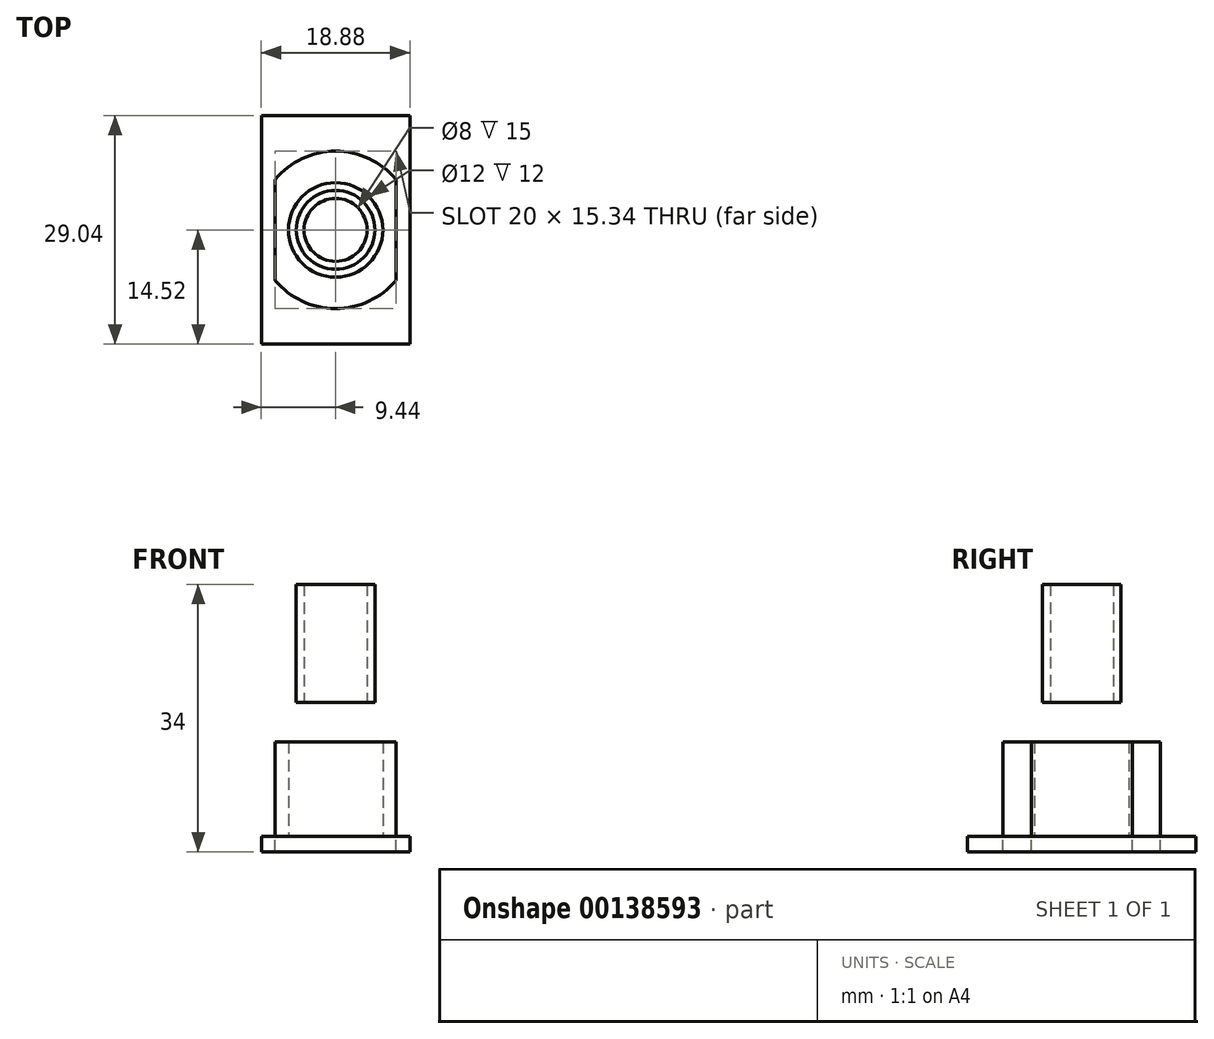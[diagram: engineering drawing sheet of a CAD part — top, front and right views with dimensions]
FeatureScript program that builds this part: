
annotation { "Feature Type Name" : "Feature", "Feature Type Description" : "" }
export const myFeature = defineFeature(function(context is Context, id is Id, definition is map)
    precondition{}
    {
        {
            var Q0;
            Q0=qCreatedBy(makeId("Top.planeOp"),FACE);
            var sketch = newSketch(context, id + "F0", { "sketchPlane" : qUnion([Q0])});
            skArc(sketch, "E0", {"start": v(-7.67, -6.42) * mm, "mid": v(0, -10) * mm, "end": v(7.67, -6.42) * mm});
            skLineSegment(sketch, "E1.left", {"start": v(7.67, 6.42) * mm, "end": v(7.67, -6.42) * mm});
            skLineSegment(sketch, "E1.right", {"start": v(-7.67, 6.42) * mm, "end": v(-7.67, -6.42) * mm});
            skArc(sketch, "E2.trimOffspring", {"start": v(7.67, 6.42) * mm, "mid": v(0, 10) * mm, "end": v(-7.67, 6.42) * mm});
            skCircle(sketch, "E3", {"center": v(0, 0) * mm, "radius": 6 * mm});
            skLineSegment(sketch, "E4.bottom", {"start": v(9.44, 14.52) * mm, "end": v(-9.44, 14.52) * mm});
            skLineSegment(sketch, "E4.top", {"start": v(9.44, -14.52) * mm, "end": v(-9.44, -14.52) * mm});
            skLineSegment(sketch, "E4.left", {"start": v(9.44, 14.52) * mm, "end": v(9.44, -14.52) * mm});
            skLineSegment(sketch, "E4.right", {"start": v(-9.44, 14.52) * mm, "end": v(-9.44, -14.52) * mm});
            skSolve(sketch);
        }
        {
            var Q0;
            Q0=makeQuery(id+"F0.imprint","IMPRINT",FACE,{"disambiguationData":[TD([[makeQuery(id+"F0.imprint","IMPRINT",EDGE,{"derivedFrom":sQuery(id+"F0.wireOp",EDGE,"E0")}),1.0]])]});
            extrude(context, id + "F1", {"entities" : qUnion([Q0]), "depth" : 12 * mm});
        }
        {
            var Q0;
            Q0=makeQuery(id+"F0.imprint","IMPRINT",FACE,{"disambiguationData":[TD([[makeQuery(id+"F0.imprint","IMPRINT",EDGE,{"derivedFrom":sQuery(id+"F0.wireOp",EDGE,"E0")}),-1.0]])]});
            extrude(context, id + "F2", {"entities" : qUnion([Q0]), "operationType" : NewBodyOperationType.ADD, "oppositeDirection" : true, "depth" : 2 * mm});
        }
        {
            var Q0;
            Q0=makeQuery(id+"F1.opExtrude","CAP_FACE",FACE,{"disambiguationData":[OSD([sQuery(id+"F0.wireOp",EDGE,"E0"),sQuery(id+"F0.wireOp",EDGE,"E1.left"),sQuery(id+"F0.wireOp",EDGE,"E1.right"),sQuery(id+"F0.wireOp",EDGE,"E2.trimOffspring"),sQuery(id+"F0.wireOp",EDGE,"E3")])],"isStart":false});
            var sketch = newSketch(context, id + "F3", { "sketchPlane" : qUnion([Q0])});
            skCircle(sketch, "E5", {"center": v(0, 0) * mm, "radius": 5 * mm});
            skCircle(sketch, "E6", {"center": v(0, 0) * mm, "radius": 4 * mm});
            skSolve(sketch);
        }
        {
            var Q0;
            Q0=makeQuery(id+"F3.imprint","IMPRINT",FACE,{"disambiguationData":[TD([[makeQuery(id+"F3.imprint","IMPRINT",EDGE,{"derivedFrom":sQuery(id+"F3.wireOp",EDGE,"E5")}),1.0]])]});
            extrude(context, id + "F4", {"entities" : qUnion([Q0]), "depth" : 15 * mm});
        }
        {
            var Q0;
            Q0=makeQuery(id+"F4.opExtrude","SWEPT_BODY",BODY,{"disambiguationData":[OSD([sQuery(id+"F3.wireOp",EDGE,"E5"),sQuery(id+"F3.wireOp",EDGE,"E6")])]});
            var Q1;
            Q1=makeQuery(id+"F4.opExtrude","CAP_EDGE",EDGE,{"disambiguationData":[OSD([sQuery(id+"F3.wireOp",EDGE,"E6")])],"isStart":false});
            transform(context, id + "F5", {"entities" : qUnion([Q0]), "transformType" : TransformType.TRANSLATION_3D, "dx" : 0 * mm, "dy" : 0 * mm, "dz" : 5 * mm, "makeCopy" : false});
        }
    });
